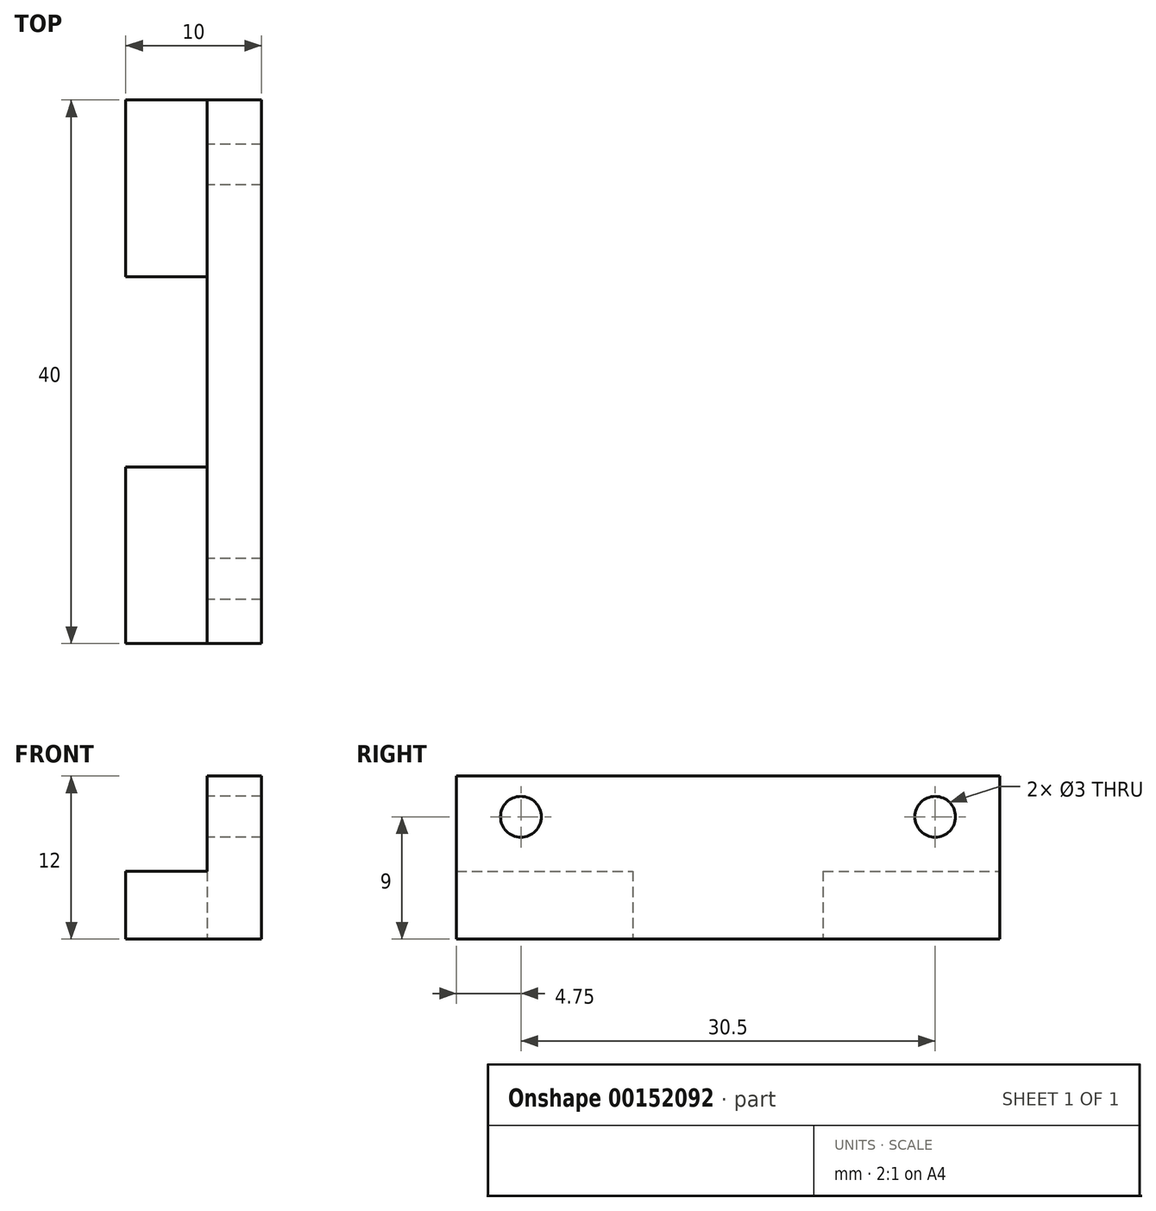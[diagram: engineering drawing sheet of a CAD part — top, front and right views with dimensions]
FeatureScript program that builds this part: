
annotation { "Feature Type Name" : "Feature", "Feature Type Description" : "" }
export const myFeature = defineFeature(function(context is Context, id is Id, definition is map)
    precondition{}
    {
        {
            var Q0;
            Q0=qCreatedBy(makeId("Front.planeOp"),FACE);
            var sketch = newSketch(context, id + "F0", { "sketchPlane" : qUnion([Q0])});
            skLineSegment(sketch, "E0", {"start": v(0, 0) * mm, "end": v(0, 5) * mm});
            skLineSegment(sketch, "E1", {"start": v(0, 5) * mm, "end": v(6, 5) * mm});
            skLineSegment(sketch, "E2", {"start": v(6, 5) * mm, "end": v(6, 12) * mm});
            skLineSegment(sketch, "E3", {"start": v(6, 12) * mm, "end": v(10, 12) * mm});
            skLineSegment(sketch, "E4", {"start": v(10, 12) * mm, "end": v(10, 0) * mm});
            skLineSegment(sketch, "E5", {"start": v(10, 0) * mm, "end": v(0, 0) * mm});
            skSolve(sketch);
        }
        {
            var Q0;
            Q0=makeQuery(id+"F0.imprint","IMPRINT",FACE,{"disambiguationData":[TD([[makeQuery(id+"F0.imprint","IMPRINT",EDGE,{"derivedFrom":sQuery(id+"F0.wireOp",EDGE,"E0")}),-1.0]])]});
            extrude(context, id + "F1", {"entities" : qUnion([Q0]), "depth" : 40 * mm});
        }
        {
            var Q0;
            Q0=makeQuery(id+"F1.opExtrude","SWEPT_FACE",FACE,{"disambiguationData":[OSD([sQuery(id+"F0.wireOp",EDGE,"E2")])]});
            var sketch = newSketch(context, id + "F2", { "sketchPlane" : qUnion([Q0])});
            skCircle(sketch, "E6", {"center": v(4.75, 9) * mm, "radius": 1.5 * mm});
            skCircle(sketch, "E7", {"center": v(35.25, 9) * mm, "radius": 1.5 * mm});
            skSolve(sketch);
        }
        {
            var Q0;
            Q0=sQuery(id+"F2.wireOp",VERTEX,"E7.center");
            var Q1;
            Q1=sQuery(id+"F2.wireOp",VERTEX,"E6.center");
            var Q2;
            Q2=makeQuery(id+"F1.opExtrude","SWEPT_BODY",BODY,{"disambiguationData":[OSD([sQuery(id+"F0.wireOp",EDGE,"E0"),sQuery(id+"F0.wireOp",EDGE,"E1"),sQuery(id+"F0.wireOp",EDGE,"E2"),sQuery(id+"F0.wireOp",EDGE,"E3"),sQuery(id+"F0.wireOp",EDGE,"E4"),sQuery(id+"F0.wireOp",EDGE,"E5")])]});
            hole(context, id + "F3", {"style" : HoleStyle.SIMPLE, "endStyle" : HoleEndStyle.THROUGH, "holeDiameter" : 3 * mm, "locations" : qUnion([Q0, Q1]), "scope" : qUnion([Q2]), "isTappedThrough" : true});
        }
        {
            var Q0;
            Q0=makeQuery(id+"F1.opExtrude","SWEPT_FACE",FACE,{"disambiguationData":[OSD([sQuery(id+"F0.wireOp",EDGE,"E5")])]});
            var sketch = newSketch(context, id + "F4", { "sketchPlane" : qUnion([Q0])});
            skLineSegment(sketch, "E8.bottom", {"start": v(6, 13) * mm, "end": v(-1.7, 13) * mm});
            skLineSegment(sketch, "E8.top", {"start": v(6, 27) * mm, "end": v(-1.7, 27) * mm});
            skLineSegment(sketch, "E8.left", {"start": v(6, 13) * mm, "end": v(6, 27) * mm});
            skLineSegment(sketch, "E8.right", {"start": v(-1.7, 13) * mm, "end": v(-1.7, 27) * mm});
            skSolve(sketch);
        }
        {
            var Q0;
            {var subQ0=sQuery(id+"F4.wireOp",EDGE,"E8.left");Q0=makeQuery(id+"F4.imprint","IMPRINT",FACE,{"disambiguationData":[TD([[makeQuery(id+"F4.imprint","IMPRINT",EDGE,{"derivedFrom":subQ0}),1.0]])]});}
            extrude(context, id + "F5", {"entities" : qUnion([Q0]), "operationType" : NewBodyOperationType.REMOVE, "oppositeDirection" : true, "depth" : 25 * mm});
        }
    });
